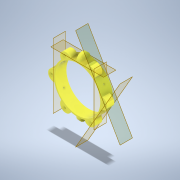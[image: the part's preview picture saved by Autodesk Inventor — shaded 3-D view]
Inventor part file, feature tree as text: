
AUTODESK INVENTOR PART (.ipt)
format: ipt  version: 2021.2 (Build 252289000, 289)  size: 317,440 bytes
history: native  units: in
note: dims shown in document units (in); Inventor stores cm internally (conversion verified against a paired STEP export)
features: extrude x11, sketch x10, plane x5, pattern_circular x4, fillet x2, mirror x1
ambient origin geometry x8: Origin, YZ Plane, XZ Plane, XY Plane, X Axis, Y Axis, Z Axis, Center Point
bodies: Solid1 (feature_tree)
feature tree (33):
  extrude  "Extrusion1"  Depth=4.25in
  plane  "Work Plane1"
  plane  "Work Plane2"
  extrude  "Extrusion3"  Depth=1.5in
  fillet  "Fillet1"  Radius=2.125in
  extrude  "Extrusion4"  TaperAngle=0.0deg  [1 undecoded]
  pattern_circular  "Circular Pattern2"  Count=2 Angle=360.0deg
  plane  "Work Plane3"
  extrude  "Extrusion8"  Depth=1.0in
  extrude  "Extrusion9"  Depth=0.25in
  fillet  "Fillet3"  [1 undecoded]
  extrude  "Extrusion10"  Depth=0.25in
  pattern_circular  "Circular Pattern4"  [2 undecoded]
  extrude  "Extrusion11"  Depth=0.25in
  mirror  "Mirror1"
  plane  "Work Plane4"
  sketch  "Sketch11"  dims[d17=0.2in]
  extrude  "Extrusion13"  Depth=0.25in
  extrude  "Extrusion14"  Depth=0.25in TaperAngle=0.0deg
  pattern_circular  "Circular Pattern5"  [2 undecoded]
  plane  "Work Plane6"
  extrude  "Extrusion15"  Depth=0.25in
  extrude  "Extrusion16"  Depth=0.25in
  pattern_circular  "Circular Pattern6"  [2 undecoded]
  sketch  "Sketch1"  dims[d0=4.0in d1=4.25in]
  sketch  "Sketch3"  dims[d2=1.0in d3=0.0in d4=1.5in d10=2.125in]
  sketch  "Sketch4"  dims[d11=0.25in d12=0.0in]
  sketch  "Sketch8"  dims[d13=0.5in d14=0.0in]
  sketch  "Sketch9"  dims[d15=0.5in]
  sketch  "Sketch10"  dims[d16=0.125in]
  sketch  "Sketch12"  dims[d18=0.5in d19=0.0in d20=0.7874in d21=360.0deg]
  sketch  "Sketch13"  dims[d23=-2.125in d24=1.0in]
  sketch  "Sketch14"  dims[d25=0.25in d26=0.5in d27=0.0in d40=0.25in d41=0.125in d42=0.25in d43=0.2in d49=0.1in d50=0.0in d51=0.5in d52=0.0in d53=0.5in d54=0.2in d55=0.25in d56=0.0in d57=0.0in d58=2.3622in d59=360.0deg d61=0.1in d62=0.0in d63=0.5in d64=0.125in d67=0.5in d68=0.5in d69=0.1in d70=0.0in d71=1.0in d72=0.0in d73=0.7874in d74=360.0deg d76=0.5in d77=0.5in d78=0.1in d79=0.0in d80=0.5in d81=0.125in d82=1.0in d83=0.0in d84=0.7874in d85=360.0deg]
note: 8 required parameter values undecoded (feature->parameter linkage not recoverable at this tier; creation-order binding heuristic only, values carry confidence <= 0.55)
